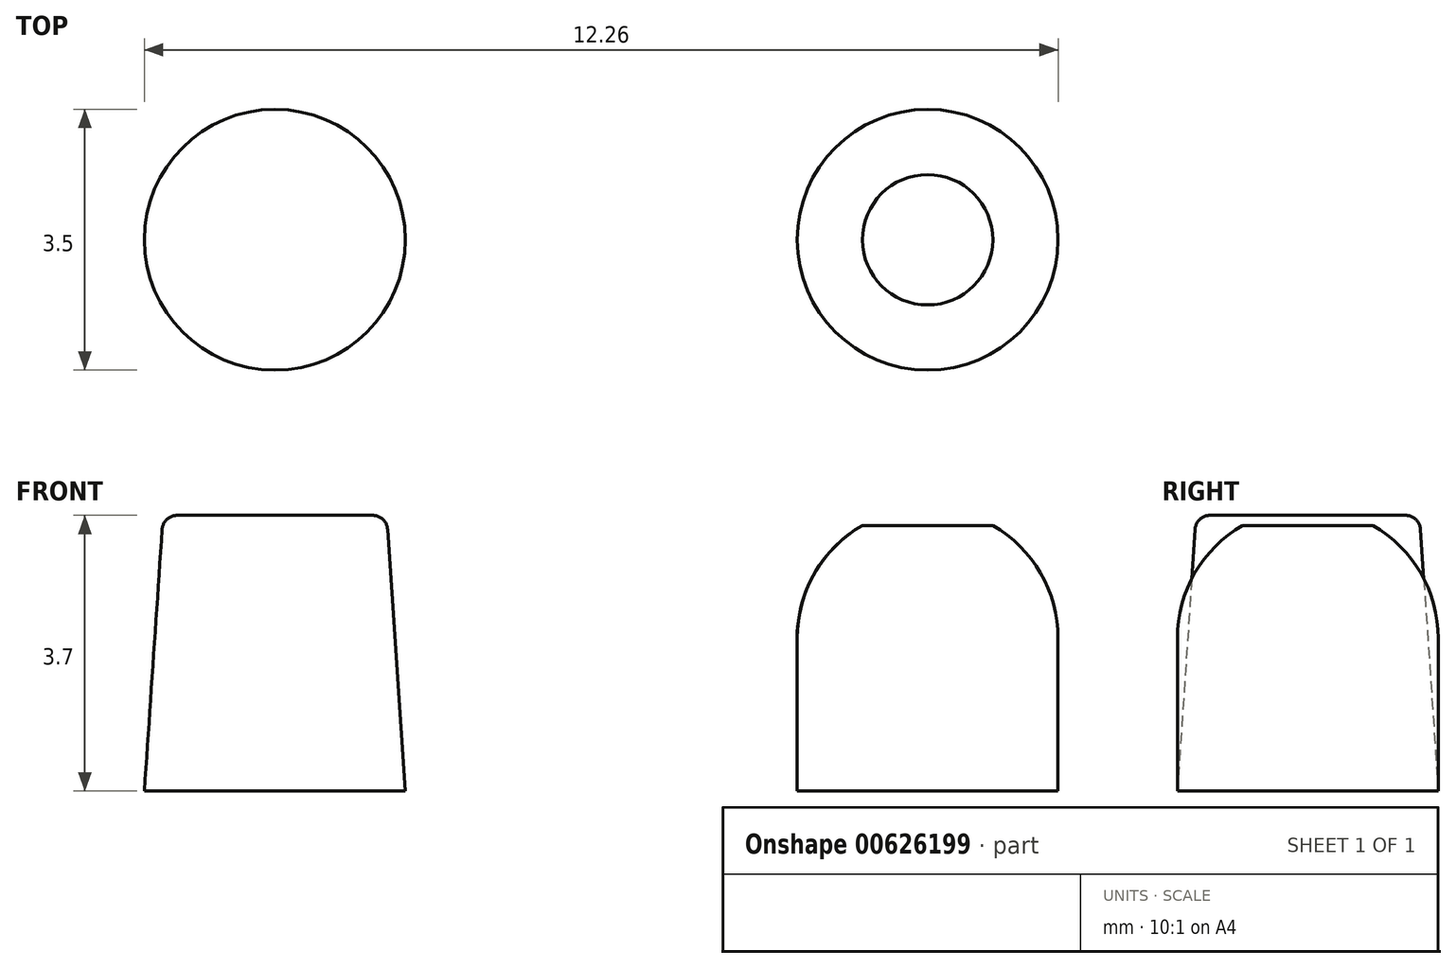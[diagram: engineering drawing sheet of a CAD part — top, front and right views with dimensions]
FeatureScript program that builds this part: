
annotation { "Feature Type Name" : "Feature", "Feature Type Description" : "" }
export const myFeature = defineFeature(function(context is Context, id is Id, definition is map)
    precondition{}
    {
        {
            var Q0;
            Q0=qCreatedBy(makeId("Front.planeOp"),FACE);
            var sketch = newSketch(context, id + "F0", { "sketchPlane" : qUnion([Q0])});
            skLineSegment(sketch, "E0", {"start": v(0, 0) * mm, "end": v(0, 3.7) * mm});
            skLineSegment(sketch, "E1", {"start": v(0, 3.7) * mm, "end": v(1.31, 3.7) * mm});
            skLineSegment(sketch, "E2", {"start": v(1.51, 3.51) * mm, "end": v(1.75, 0) * mm});
            skLineSegment(sketch, "E3", {"start": v(1.75, 0) * mm, "end": v(0, 0) * mm});
            skPoint(sketch, "E4.visualSharp", {"position": v(1.5, 3.7) * mm});
            skArc(sketch, "E4.filletArc", {"start": v(1.51, 3.51) * mm, "mid": v(1.45, 3.65) * mm, "end": v(1.31, 3.7) * mm});
            skSolve(sketch);
        }
        {
            var Q0;
            Q0=makeQuery(id+"F0.imprint","IMPRINT",FACE,{"disambiguationData":[TD([[makeQuery(id+"F0.imprint","IMPRINT",EDGE,{"derivedFrom":sQuery(id+"F0.wireOp",EDGE,"E0")}),-1.0]])]});
            var Q1;
            Q1=sQuery(id+"F0.wireOp",EDGE,"E0");
            revolve(context, id + "F1", {"entities" : qUnion([Q0]), "axis" : qUnion([Q1]), "revolveType" : RevolveType.FULL});
        }
        {
            var Q0;
            Q0=qCreatedBy(makeId("Front.planeOp"),FACE);
            var sketch = newSketch(context, id + "F2", { "sketchPlane" : qUnion([Q0])});
            skLineSegment(sketch, "E5", {"start": v(8.76, 0) * mm, "end": v(8.76, 2.05) * mm});
            skLineSegment(sketch, "E6", {"start": v(10.5, 2.05) * mm, "end": v(10.5, 0) * mm});
            skLineSegment(sketch, "E7", {"start": v(10.5, 0) * mm, "end": v(8.76, 0) * mm});
            skLineSegment(sketch, "E8", {"start": v(8.76, 2.05) * mm, "end": v(8.76, 3.57) * mm});
            skArc(sketch, "E9", {"start": v(10.5, 2.05) * mm, "mid": v(10.27, 2.92) * mm, "end": v(9.63, 3.57) * mm});
            skLineSegment(sketch, "E10", {"start": v(9.63, 3.57) * mm, "end": v(8.76, 3.57) * mm});
            skSolve(sketch);
        }
        {
            var Q0;
            Q0 = qSketchRegion(id + "F2", true);
            var Q1;
            Q1=sQuery(id+"F2.wireOp",EDGE,"E5");
            revolve(context, id + "F3", {"entities" : qUnion([Q0]), "axis" : qUnion([Q1]), "revolveType" : RevolveType.FULL});
        }
    });
